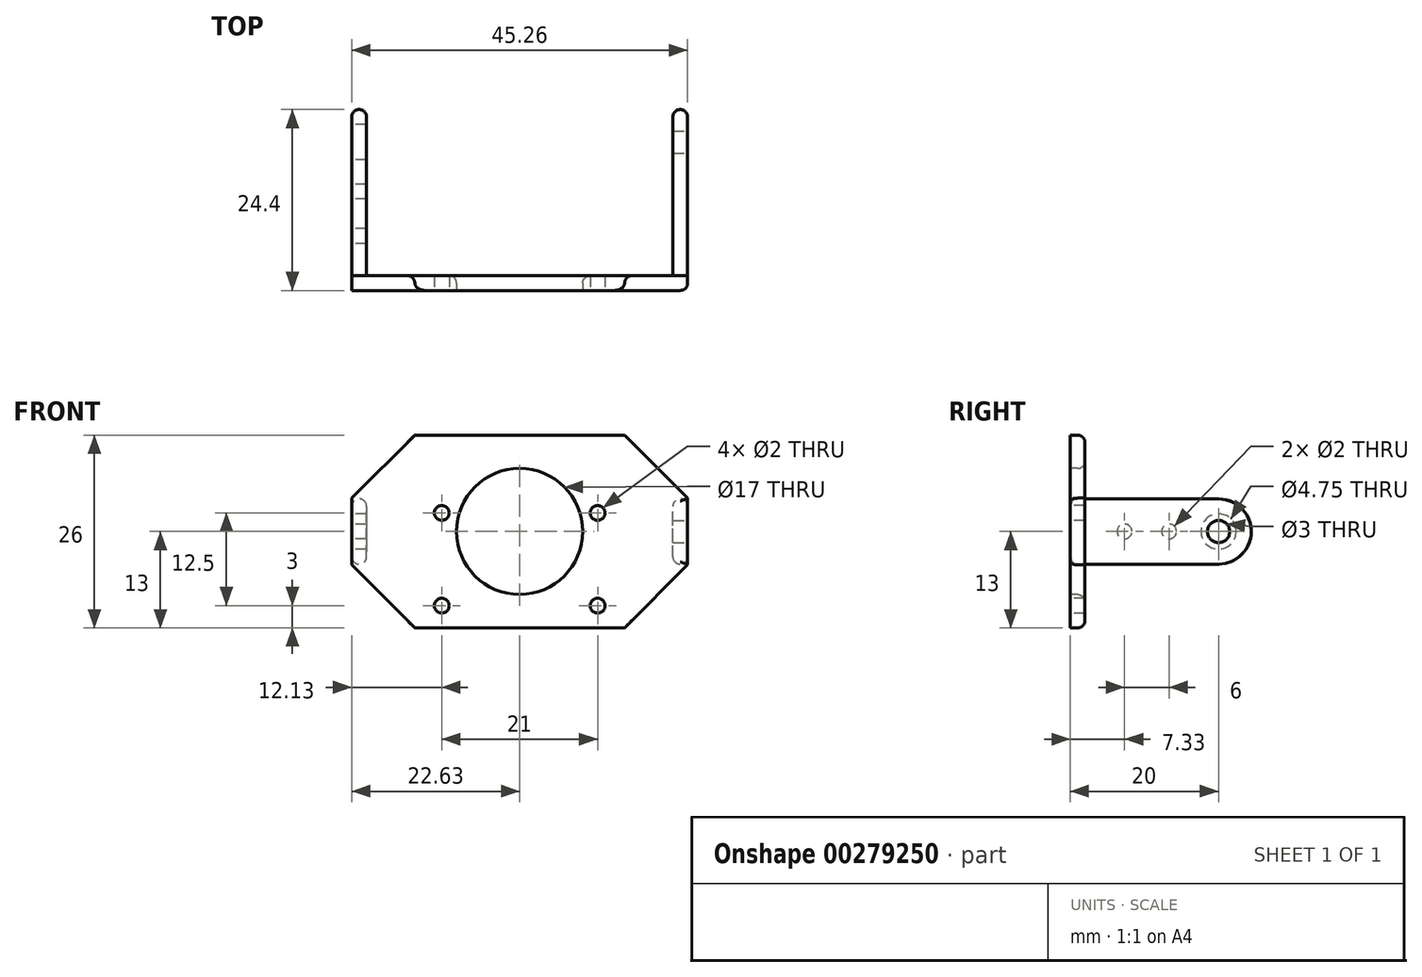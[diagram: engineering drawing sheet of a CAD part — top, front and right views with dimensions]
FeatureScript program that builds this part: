
annotation { "Feature Type Name" : "Feature", "Feature Type Description" : "" }
export const myFeature = defineFeature(function(context is Context, id is Id, definition is map)
    precondition{}
    {
        {
            var Q0;
            Q0=qCreatedBy(makeId("Front.planeOp"),FACE);
            var sketch = newSketch(context, id + "F0", { "sketchPlane" : qUnion([Q0])});
            skLineSegment(sketch, "E0.bottom", {"start": v(-22.62, -13) * mm, "end": v(22.63, -13) * mm});
            skLineSegment(sketch, "E0.top", {"start": v(-22.63, 13) * mm, "end": v(22.62, 13) * mm});
            skLineSegment(sketch, "E0.left", {"start": v(-22.62, -13) * mm, "end": v(-22.63, 13) * mm});
            skLineSegment(sketch, "E0.right", {"start": v(22.63, -13) * mm, "end": v(22.62, 13) * mm});
            skPoint(sketch, "E0.middle", {"position": v(0, 0) * mm});
            skLineSegment(sketch, "E1.bottom", {"start": v(12.5, -12) * mm, "end": v(-12.5, -12) * mm});
            skLineSegment(sketch, "E1.top", {"start": v(12.5, 12) * mm, "end": v(-12.5, 12) * mm});
            skLineSegment(sketch, "E1.left", {"start": v(12.5, -12) * mm, "end": v(12.5, 12) * mm});
            skLineSegment(sketch, "E1.right", {"start": v(-12.5, -12) * mm, "end": v(-12.5, 12) * mm});
            skCircle(sketch, "E2", {"center": v(-10.5, -10) * mm, "radius": 1 * mm});
            skCircle(sketch, "E3.MirrorC", {"center": v(10.5, -10) * mm, "radius": 1 * mm});
            skCircle(sketch, "E4", {"center": v(-10.5, 2.5) * mm, "radius": 1 * mm});
            skCircle(sketch, "E5.MirrorC", {"center": v(10.5, 2.5) * mm, "radius": 1 * mm});
            skCircle(sketch, "E6", {"center": v(0, 0) * mm, "radius": 8.5 * mm});
            skSolve(sketch);
        }
        {
            var Q0;
            Q0=makeQuery(id+"F0.imprint","IMPRINT",FACE,{"disambiguationData":[TD([[makeQuery(id+"F0.imprint","IMPRINT",EDGE,{"derivedFrom":sQuery(id+"F0.wireOp",EDGE,"E0.bottom")}),1.0]])]});
            var Q1;
            Q1=makeQuery(id+"F0.imprint","IMPRINT",FACE,{"disambiguationData":[TD([[makeQuery(id+"F0.imprint","IMPRINT",EDGE,{"derivedFrom":sQuery(id+"F0.wireOp",EDGE,"E1.bottom")}),-1.0]])]});
            extrude(context, id + "F1", {"entities" : qUnion([Q0, Q1]), "oppositeDirection" : true, "depth" : 2 * mm});
        }
        {
            var Q0;
            Q0=makeQuery(id+"F1.opExtrude","SWEPT_FACE",FACE,{"disambiguationData":[OSD([sQuery(id+"F0.wireOp",EDGE,"E0.right")])]});
            var sketch = newSketch(context, id + "F2", { "sketchPlane" : qUnion([Q0])});
            skCircle(sketch, "E7", {"center": v(20, 0) * mm, "radius": 1.5 * mm});
            skCircle(sketch, "E8", {"center": v(20, 0) * mm, "radius": 4.4 * mm});
            skLineSegment(sketch, "E9.bottom", {"start": v(20, -4.4) * mm, "end": v(2, -4.4) * mm});
            skLineSegment(sketch, "E9.top", {"start": v(20, 4.4) * mm, "end": v(2, 4.4) * mm});
            skLineSegment(sketch, "E9.left", {"start": v(20, -4.4) * mm, "end": v(20, 4.4) * mm});
            skLineSegment(sketch, "E9.right", {"start": v(2, -4.4) * mm, "end": v(2, 4.4) * mm});
            skSolve(sketch);
        }
        {
            var Q0;
            {var subQ1=sQuery(id+"F2.wireOp",EDGE,"E9.bottom");Q0=makeQuery(id+"F2.imprint","IMPRINT",FACE,{"disambiguationData":[TD([[makeQuery(id+"F2.imprint","IMPRINT",EDGE,{"derivedFrom":subQ1}),-1.0]])]});}
            var Q1;
            {var subQ0=sQuery(id+"F2.wireOp",EDGE,"E9.left");var subQ1=sQuery(id+"F2.wireOp",EDGE,"E7");var subQ2=makeQuery(id+"F2.imprint","INTERSECT",VERTEX,{"disambiguationData":[OD(0.0)],"derivedFrom":[subQ1,subQ0]});Q1=makeQuery(id+"F2.imprint","IMPRINT",FACE,{"disambiguationData":[TD([[makeQuery(id+"F2.imprint","IMPRINT",EDGE,{"disambiguationData":[TD([[subQ2,1.0]])],"derivedFrom":subQ1}),-1.0]])]});}
            var Q2;
            {var subQ0=sQuery(id+"F2.wireOp",EDGE,"E9.left");var subQ1=sQuery(id+"F2.wireOp",EDGE,"E7");var subQ2=makeQuery(id+"F2.imprint","INTERSECT",VERTEX,{"disambiguationData":[OD(0.0)],"derivedFrom":[subQ1,subQ0]});Q2=makeQuery(id+"F2.imprint","IMPRINT",FACE,{"disambiguationData":[TD([[makeQuery(id+"F2.imprint","IMPRINT",EDGE,{"disambiguationData":[TD([[subQ2,-1.0]])],"derivedFrom":subQ1}),-1.0]])]});}
            extrude(context, id + "F3", {"entities" : qUnion([Q0, Q1, Q2]), "oppositeDirection" : true, "depth" : 2 * mm});
        }
        {
            var Q0;
            Q0=makeQuery(id+"F1.opExtrude","SWEPT_FACE",FACE,{"disambiguationData":[OSD([sQuery(id+"F0.wireOp",EDGE,"E0.left")])]});
            var sketch = newSketch(context, id + "F4", { "sketchPlane" : qUnion([Q0])});
            skCircle(sketch, "E10", {"center": v(-20, 0) * mm, "radius": 2.37 * mm});
            skCircle(sketch, "E11", {"center": v(-20, 0) * mm, "radius": 4.4 * mm});
            skLineSegment(sketch, "E12.bottom", {"start": v(-2, 4.4) * mm, "end": v(-20, 4.4) * mm});
            skLineSegment(sketch, "E12.top", {"start": v(-2, -4.4) * mm, "end": v(-20, -4.4) * mm});
            skLineSegment(sketch, "E12.left", {"start": v(-2, 4.4) * mm, "end": v(-2, -4.4) * mm});
            skLineSegment(sketch, "E12.right", {"start": v(-20, 4.4) * mm, "end": v(-20, -4.4) * mm});
            skCircle(sketch, "E13", {"center": v(-13.33, 0) * mm, "radius": 1 * mm});
            skCircle(sketch, "E14", {"center": v(-7.33, 0) * mm, "radius": 1 * mm});
            skSolve(sketch);
        }
        {
            var Q0;
            {var subQ0=sQuery(id+"F4.wireOp",EDGE,"E12.right");var subQ1=sQuery(id+"F4.wireOp",EDGE,"E10");var subQ2=makeQuery(id+"F4.imprint","INTERSECT",VERTEX,{"disambiguationData":[OD(0.0)],"derivedFrom":[subQ1,subQ0]});Q0=makeQuery(id+"F4.imprint","IMPRINT",FACE,{"disambiguationData":[TD([[makeQuery(id+"F4.imprint","IMPRINT",EDGE,{"disambiguationData":[TD([[subQ2,-1.0]])],"derivedFrom":subQ1}),-1.0]])]});}
            var Q1;
            {var subQ0=sQuery(id+"F4.wireOp",EDGE,"E12.right");var subQ1=sQuery(id+"F4.wireOp",EDGE,"E10");var subQ2=makeQuery(id+"F4.imprint","INTERSECT",VERTEX,{"disambiguationData":[OD(0.0)],"derivedFrom":[subQ1,subQ0]});Q1=makeQuery(id+"F4.imprint","IMPRINT",FACE,{"disambiguationData":[TD([[makeQuery(id+"F4.imprint","IMPRINT",EDGE,{"disambiguationData":[TD([[subQ2,1.0]])],"derivedFrom":subQ1}),-1.0]])]});}
            var Q2;
            {var subQ1=sQuery(id+"F4.wireOp",EDGE,"E12.bottom");Q2=makeQuery(id+"F4.imprint","IMPRINT",FACE,{"disambiguationData":[TD([[makeQuery(id+"F4.imprint","IMPRINT",EDGE,{"derivedFrom":subQ1}),1.0]])]});}
            extrude(context, id + "F5", {"entities" : qUnion([Q0, Q1, Q2]), "oppositeDirection" : true, "depth" : 2 * mm});
        }
        {
            var Q0;
            Q0=makeQuery(id+"F1.opExtrude","SWEPT_EDGE",EDGE,{"disambiguationData":[OSD([sQuery(id+"F0.wireOp",EDGE,"E0.top"),sQuery(id+"F0.wireOp",EDGE,"E0.right")])]});
            var Q1;
            Q1=makeQuery(id+"F1.opExtrude","SWEPT_EDGE",EDGE,{"disambiguationData":[OSD([sQuery(id+"F0.wireOp",EDGE,"E0.top"),sQuery(id+"F0.wireOp",EDGE,"E0.left")])]});
            var Q2;
            Q2=makeQuery(id+"F1.opExtrude","SWEPT_EDGE",EDGE,{"disambiguationData":[OSD([sQuery(id+"F0.wireOp",EDGE,"E0.bottom"),sQuery(id+"F0.wireOp",EDGE,"E0.left")])]});
            var Q3;
            Q3=makeQuery(id+"F1.opExtrude","SWEPT_EDGE",EDGE,{"disambiguationData":[OSD([sQuery(id+"F0.wireOp",EDGE,"E0.bottom"),sQuery(id+"F0.wireOp",EDGE,"E0.right")])]});
            chamfer(context, id + "F6", {"entities" : qUnion([Q0, Q1, Q2, Q3]), "width" : 8.5 * mm, "tangentPropagation" : true});
        }
        {
            var Q0;
            Q0=makeQuery(id+"F1.opExtrude","CAP_EDGE",EDGE,{"disambiguationData":[OSD([sQuery(id+"F0.wireOp",EDGE,"E6")])],"isStart":false});
            var Q1;
            {var subQ0=sQuery(id+"F0.wireOp",EDGE,"E0.right");var subQ1=sQuery(id+"F0.wireOp",EDGE,"E0.top");Q1=makeQuery(id+"F6.opChamfer","BLEND_EDGE",EDGE,{"blendedFrom":[makeQuery(id+"F1.opExtrude","SWEPT_EDGE",EDGE,{"disambiguationData":[OSD([subQ1,subQ0])]}),makeQuery(id+"F1.opExtrude","CAP_FACE",FACE,{"disambiguationData":[OSD([sQuery(id+"F0.wireOp",EDGE,"E0.bottom"),subQ1,sQuery(id+"F0.wireOp",EDGE,"E0.left"),subQ0,sQuery(id+"F0.wireOp",EDGE,"E2"),sQuery(id+"F0.wireOp",EDGE,"E3.MirrorC"),sQuery(id+"F0.wireOp",EDGE,"E4"),sQuery(id+"F0.wireOp",EDGE,"E5.MirrorC"),sQuery(id+"F0.wireOp",EDGE,"E6")])],"isStart":true})],"blendedInto":[makeQuery(id+"F1.opExtrude","CAP_FACE",FACE,{"disambiguationData":[OSD([sQuery(id+"F0.wireOp",EDGE,"E0.bottom"),subQ1,sQuery(id+"F0.wireOp",EDGE,"E0.left"),subQ0,sQuery(id+"F0.wireOp",EDGE,"E2"),sQuery(id+"F0.wireOp",EDGE,"E3.MirrorC"),sQuery(id+"F0.wireOp",EDGE,"E4"),sQuery(id+"F0.wireOp",EDGE,"E5.MirrorC"),sQuery(id+"F0.wireOp",EDGE,"E6")])],"isStart":true})]});}
            var Q2;
            {var subQ0=sQuery(id+"F0.wireOp",EDGE,"E0.right");var subQ1=sQuery(id+"F0.wireOp",EDGE,"E0.bottom");Q2=makeQuery(id+"F6.opChamfer","BLEND_EDGE",EDGE,{"blendedFrom":[makeQuery(id+"F1.opExtrude","SWEPT_EDGE",EDGE,{"disambiguationData":[OSD([subQ1,subQ0])]}),makeQuery(id+"F1.opExtrude","CAP_FACE",FACE,{"disambiguationData":[OSD([subQ1,sQuery(id+"F0.wireOp",EDGE,"E0.top"),sQuery(id+"F0.wireOp",EDGE,"E0.left"),subQ0,sQuery(id+"F0.wireOp",EDGE,"E2"),sQuery(id+"F0.wireOp",EDGE,"E3.MirrorC"),sQuery(id+"F0.wireOp",EDGE,"E4"),sQuery(id+"F0.wireOp",EDGE,"E5.MirrorC"),sQuery(id+"F0.wireOp",EDGE,"E6")])],"isStart":true})],"blendedInto":[makeQuery(id+"F1.opExtrude","CAP_FACE",FACE,{"disambiguationData":[OSD([subQ1,sQuery(id+"F0.wireOp",EDGE,"E0.top"),sQuery(id+"F0.wireOp",EDGE,"E0.left"),subQ0,sQuery(id+"F0.wireOp",EDGE,"E2"),sQuery(id+"F0.wireOp",EDGE,"E3.MirrorC"),sQuery(id+"F0.wireOp",EDGE,"E4"),sQuery(id+"F0.wireOp",EDGE,"E5.MirrorC"),sQuery(id+"F0.wireOp",EDGE,"E6")])],"isStart":true})]});}
            var Q3;
            Q3=makeQuery(id+"F1.opExtrude","CAP_EDGE",EDGE,{"disambiguationData":[OSD([sQuery(id+"F0.wireOp",EDGE,"E0.right")])],"isStart":true});
            var Q4;
            {var subQ0=sQuery(id+"F0.wireOp",EDGE,"E0.left");var subQ1=sQuery(id+"F0.wireOp",EDGE,"E0.bottom");Q4=makeQuery(id+"F6.opChamfer","BLEND_EDGE",EDGE,{"blendedFrom":[makeQuery(id+"F1.opExtrude","SWEPT_EDGE",EDGE,{"disambiguationData":[OSD([subQ1,subQ0])]}),makeQuery(id+"F1.opExtrude","CAP_FACE",FACE,{"disambiguationData":[OSD([subQ1,sQuery(id+"F0.wireOp",EDGE,"E0.top"),subQ0,sQuery(id+"F0.wireOp",EDGE,"E0.right"),sQuery(id+"F0.wireOp",EDGE,"E2"),sQuery(id+"F0.wireOp",EDGE,"E3.MirrorC"),sQuery(id+"F0.wireOp",EDGE,"E4"),sQuery(id+"F0.wireOp",EDGE,"E5.MirrorC"),sQuery(id+"F0.wireOp",EDGE,"E6")])],"isStart":true})],"blendedInto":[makeQuery(id+"F1.opExtrude","CAP_FACE",FACE,{"disambiguationData":[OSD([subQ1,sQuery(id+"F0.wireOp",EDGE,"E0.top"),subQ0,sQuery(id+"F0.wireOp",EDGE,"E0.right"),sQuery(id+"F0.wireOp",EDGE,"E2"),sQuery(id+"F0.wireOp",EDGE,"E3.MirrorC"),sQuery(id+"F0.wireOp",EDGE,"E4"),sQuery(id+"F0.wireOp",EDGE,"E5.MirrorC"),sQuery(id+"F0.wireOp",EDGE,"E6")])],"isStart":true})]});}
            var Q5;
            {var subQ0=sQuery(id+"F0.wireOp",EDGE,"E0.left");var subQ1=sQuery(id+"F0.wireOp",EDGE,"E0.top");Q5=makeQuery(id+"F6.opChamfer","BLEND_EDGE",EDGE,{"blendedFrom":[makeQuery(id+"F1.opExtrude","SWEPT_EDGE",EDGE,{"disambiguationData":[OSD([subQ1,subQ0])]}),makeQuery(id+"F1.opExtrude","CAP_FACE",FACE,{"disambiguationData":[OSD([sQuery(id+"F0.wireOp",EDGE,"E0.bottom"),subQ1,subQ0,sQuery(id+"F0.wireOp",EDGE,"E0.right"),sQuery(id+"F0.wireOp",EDGE,"E2"),sQuery(id+"F0.wireOp",EDGE,"E3.MirrorC"),sQuery(id+"F0.wireOp",EDGE,"E4"),sQuery(id+"F0.wireOp",EDGE,"E5.MirrorC"),sQuery(id+"F0.wireOp",EDGE,"E6")])],"isStart":true})],"blendedInto":[makeQuery(id+"F1.opExtrude","CAP_FACE",FACE,{"disambiguationData":[OSD([sQuery(id+"F0.wireOp",EDGE,"E0.bottom"),subQ1,subQ0,sQuery(id+"F0.wireOp",EDGE,"E0.right"),sQuery(id+"F0.wireOp",EDGE,"E2"),sQuery(id+"F0.wireOp",EDGE,"E3.MirrorC"),sQuery(id+"F0.wireOp",EDGE,"E4"),sQuery(id+"F0.wireOp",EDGE,"E5.MirrorC"),sQuery(id+"F0.wireOp",EDGE,"E6")])],"isStart":true})]});}
            var Q6;
            Q6=makeQuery(id+"F5.opExtrude","CAP_EDGE",EDGE,{"disambiguationData":[OSD([sQuery(id+"F4.wireOp",EDGE,"E12.top")])],"isStart":true});
            var Q7;
            Q7=makeQuery(id+"F3.opExtrude","CAP_EDGE",EDGE,{"disambiguationData":[OSD([sQuery(id+"F2.wireOp",EDGE,"E9.top")])],"isStart":true});
            var Q8;
            Q8=makeQuery(id+"F1.opExtrude","CAP_EDGE",EDGE,{"disambiguationData":[OSD([sQuery(id+"F0.wireOp",EDGE,"E0.bottom")])],"isStart":false});
            var Q9;
            Q9=makeQuery(id+"F1.opExtrude","CAP_EDGE",EDGE,{"disambiguationData":[OSD([sQuery(id+"F0.wireOp",EDGE,"E0.top")])],"isStart":false});
            var Q10;
            Q10=makeQuery(id+"F5.opExtrude","CAP_EDGE",EDGE,{"disambiguationData":[OSD([sQuery(id+"F4.wireOp",EDGE,"E12.bottom")])],"isStart":false});
            var Q11;
            Q11=makeQuery(id+"F3.opExtrude","CAP_EDGE",EDGE,{"disambiguationData":[OSD([sQuery(id+"F2.wireOp",EDGE,"E9.top")])],"isStart":false});
            fillet(context, id + "F7", {"entities" : qUnion([Q0, Q1, Q2, Q3, Q4, Q5, Q6, Q7, Q8, Q9, Q10, Q11]), "radius" : 1 * mm, "tangentPropagation" : true, "allowEdgeOverflow" : false});
        }
    });
